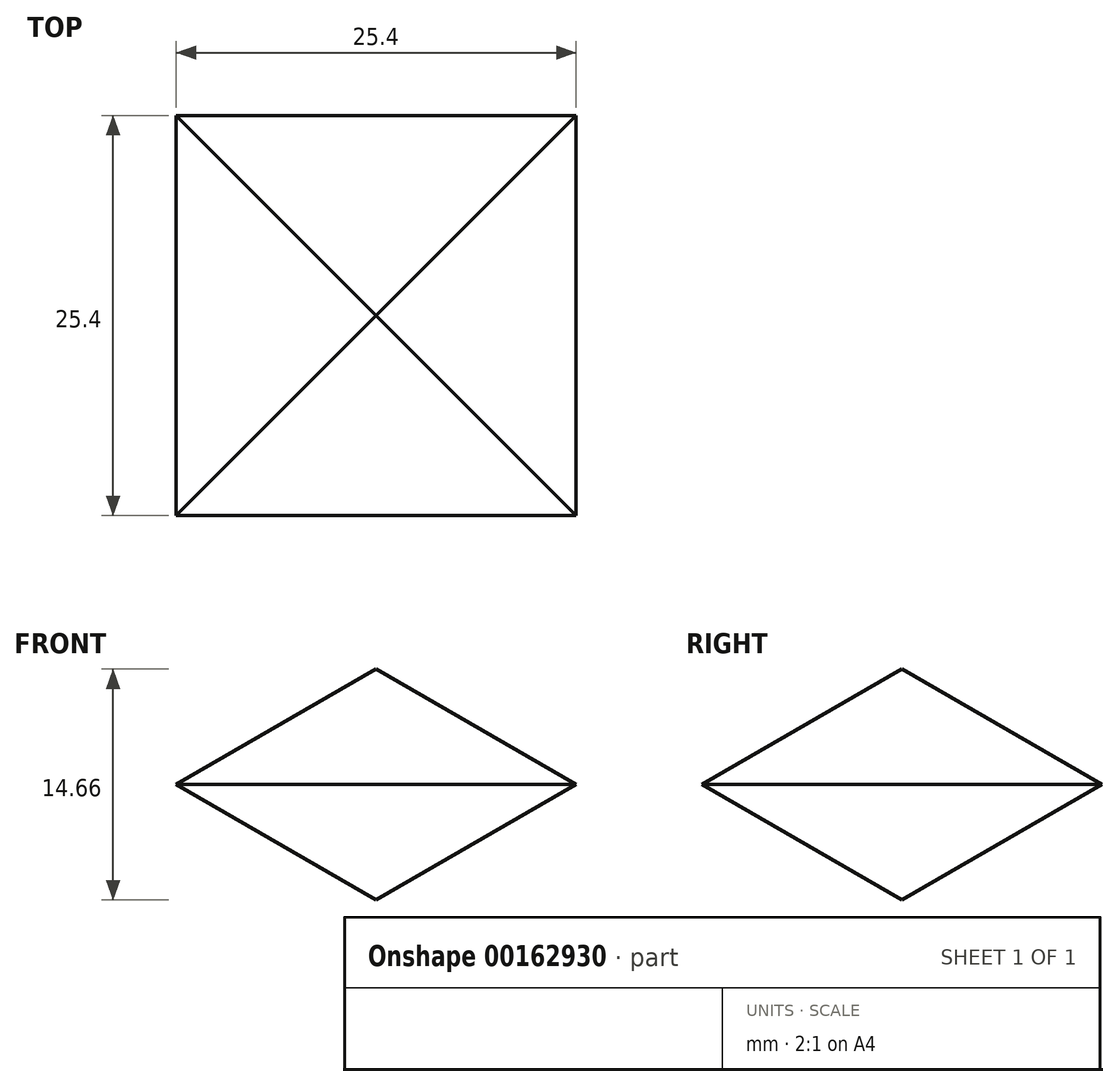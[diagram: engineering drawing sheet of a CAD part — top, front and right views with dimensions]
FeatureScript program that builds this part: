
annotation { "Feature Type Name" : "Feature", "Feature Type Description" : "" }
export const myFeature = defineFeature(function(context is Context, id is Id, definition is map)
    precondition{}
    {
        {
            var Q0;
            Q0=qCreatedBy(makeId("Top.planeOp"),FACE);
            var sketch = newSketch(context, id + "F0", { "sketchPlane" : qUnion([Q0])});
            skLineSegment(sketch, "E0.bottom", {"start": v(-12.7, 12.7) * mm, "end": v(12.7, 12.7) * mm});
            skLineSegment(sketch, "E0.top", {"start": v(-12.7, -12.7) * mm, "end": v(12.7, -12.7) * mm});
            skLineSegment(sketch, "E0.left", {"start": v(-12.7, 12.7) * mm, "end": v(-12.7, -12.7) * mm});
            skLineSegment(sketch, "E0.right", {"start": v(12.7, 12.7) * mm, "end": v(12.7, -12.7) * mm});
            skPoint(sketch, "E0.middle", {"position": v(0, 0) * mm});
            skSolve(sketch);
        }
        {
            var Q0;
            Q0=makeQuery(id+"F0.imprint","IMPRINT",FACE,{"disambiguationData":[TD([[makeQuery(id+"F0.imprint","IMPRINT",EDGE,{"derivedFrom":sQuery(id+"F0.wireOp",EDGE,"E0.bottom")}),-1.0]])]});
            extrude(context, id + "F1", {"entities" : qUnion([Q0]), "depth" : 25.4 * mm, "hasDraft" : true, "draftAngle" : 60 * degree, "draftPullDirection" : true, "hasSecondDirection" : true, "secondDirectionOppositeDirection" : true, "secondDirectionDepth" : 25.4 * mm, "hasSecondDirectionDraft" : true, "secondDirectionDraftAngle" : 60 * degree, "secondDirectionDraftPullDirection" : true});
        }
    });
